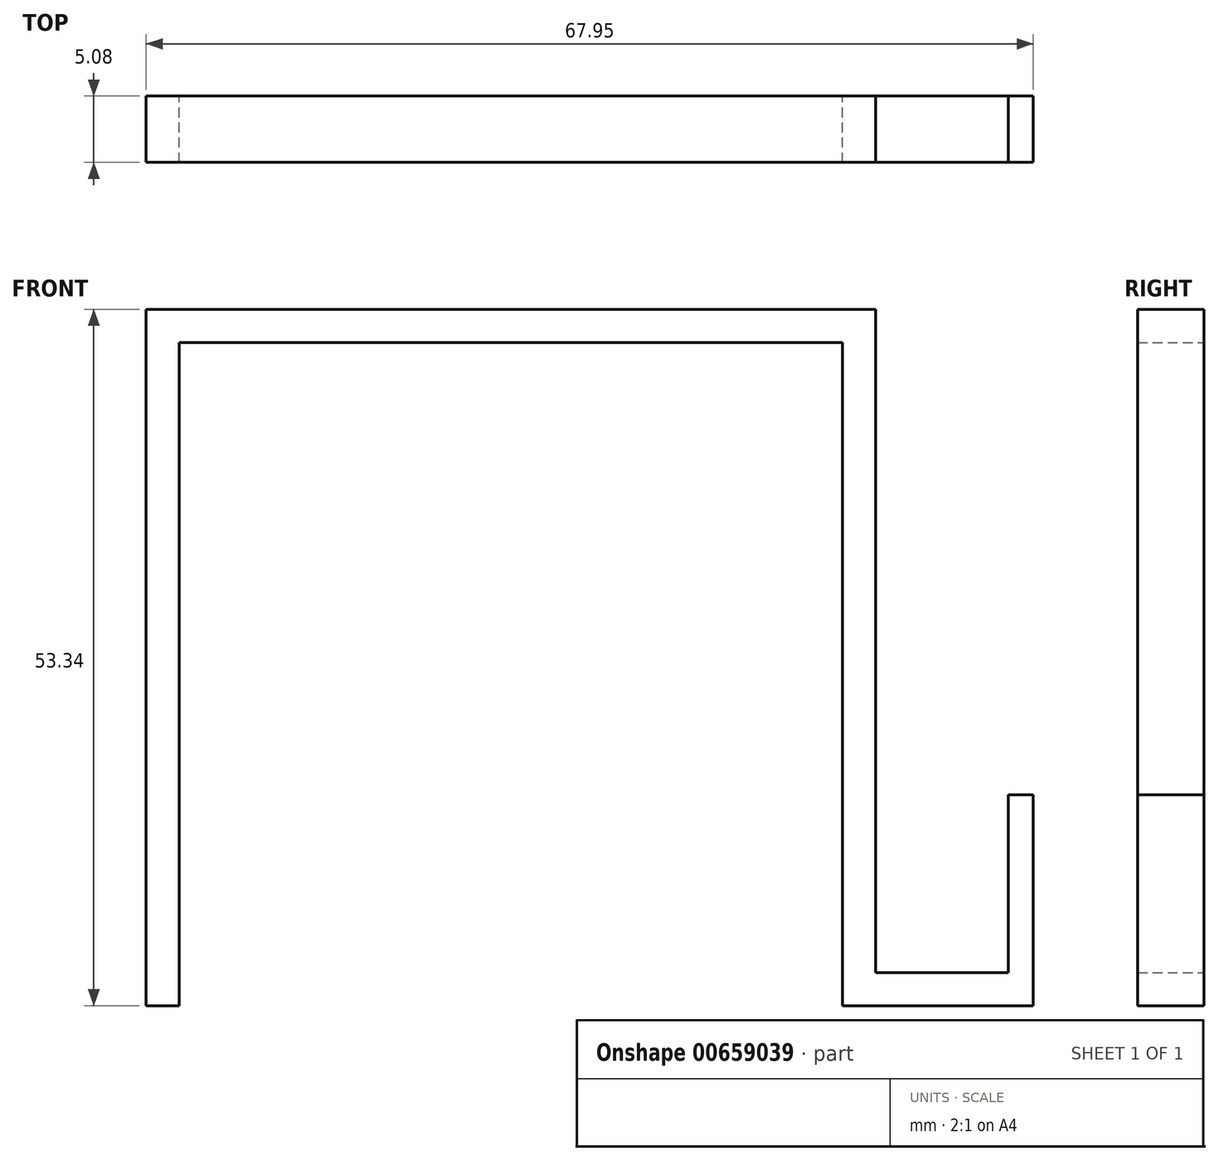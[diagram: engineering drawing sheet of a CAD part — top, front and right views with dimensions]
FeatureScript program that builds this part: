
annotation { "Feature Type Name" : "Feature", "Feature Type Description" : "" }
export const myFeature = defineFeature(function(context is Context, id is Id, definition is map)
    precondition{}
    {
        {
            var Q0;
            Q0=qCreatedBy(makeId("Front.planeOp"),FACE);
            var sketch = newSketch(context, id + "F0", { "sketchPlane" : qUnion([Q0])});
            skLineSegment(sketch, "E0", {"start": v(-40.37, 0) * mm, "end": v(-40.37, 50.8) * mm});
            skLineSegment(sketch, "E1", {"start": v(-40.37, 50.8) * mm, "end": v(10.43, 50.8) * mm});
            skLineSegment(sketch, "E2", {"start": v(10.43, 50.8) * mm, "end": v(10.43, 0) * mm});
            skLineSegment(sketch, "E3", {"start": v(10.43, 0) * mm, "end": v(25.04, 0) * mm});
            skLineSegment(sketch, "E4", {"start": v(25.04, 0) * mm, "end": v(25.04, 16.15) * mm});
            skLineSegment(sketch, "E5", {"start": v(25.04, 16.15) * mm, "end": v(23.13, 16.15) * mm});
            skLineSegment(sketch, "E6", {"start": v(23.13, 16.15) * mm, "end": v(23.13, 2.54) * mm});
            skLineSegment(sketch, "E7", {"start": v(23.13, 2.54) * mm, "end": v(12.97, 2.54) * mm});
            skLineSegment(sketch, "E8", {"start": v(12.97, 2.54) * mm, "end": v(12.97, 53.34) * mm});
            skLineSegment(sketch, "E9", {"start": v(12.97, 53.34) * mm, "end": v(-42.9, 53.34) * mm});
            skLineSegment(sketch, "E10", {"start": v(-42.9, 53.34) * mm, "end": v(-42.9, 0) * mm});
            skLineSegment(sketch, "E11", {"start": v(-42.9, 0) * mm, "end": v(-40.37, 0) * mm});
            skSolve(sketch);
        }
        {
            var Q0;
            Q0=makeQuery(id+"F0.imprint","IMPRINT",FACE,{"disambiguationData":[TD([[makeQuery(id+"F0.imprint","IMPRINT",EDGE,{"derivedFrom":sQuery(id+"F0.wireOp",EDGE,"E0")}),1.0]])]});
            extrude(context, id + "F1", {"entities" : qUnion([Q0]), "depth" : 5.08 * mm, "offsetDistance" : 25.4 * mm});
        }
    });
